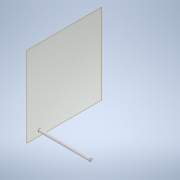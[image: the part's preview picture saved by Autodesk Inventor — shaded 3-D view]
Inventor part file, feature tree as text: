
AUTODESK INVENTOR PART (.ipt)
format: ipt  version: 2021 (Build 250183000, 183)  size: 114,688 bytes
history: native  units: mm
features: extrude x5, sketch x5, other x1
ambient origin geometry x8: Origin, YZ Plane, XZ Plane, XY Plane, X Axis, Y Axis, Z Axis, Center Point
bodies: Body1 (feature_tree)
feature tree (11):
  other  "作業平面1"
  extrude  "押し出し12"  Depth=12000.0mm
  extrude  "押し出し13"  Depth=80.0mm
  extrude  "押し出し14"  Depth=100.0mm
  extrude  "押し出し15"  Depth=530.0mm
  extrude  "押し出し16"  Depth=1500.0mm TaperAngle=0.0deg
  sketch  "スケッチ13"
  sketch  "スケッチ14"
  sketch  "スケッチ15"
  sketch  "スケッチ16"
  sketch  "スケッチ17"
